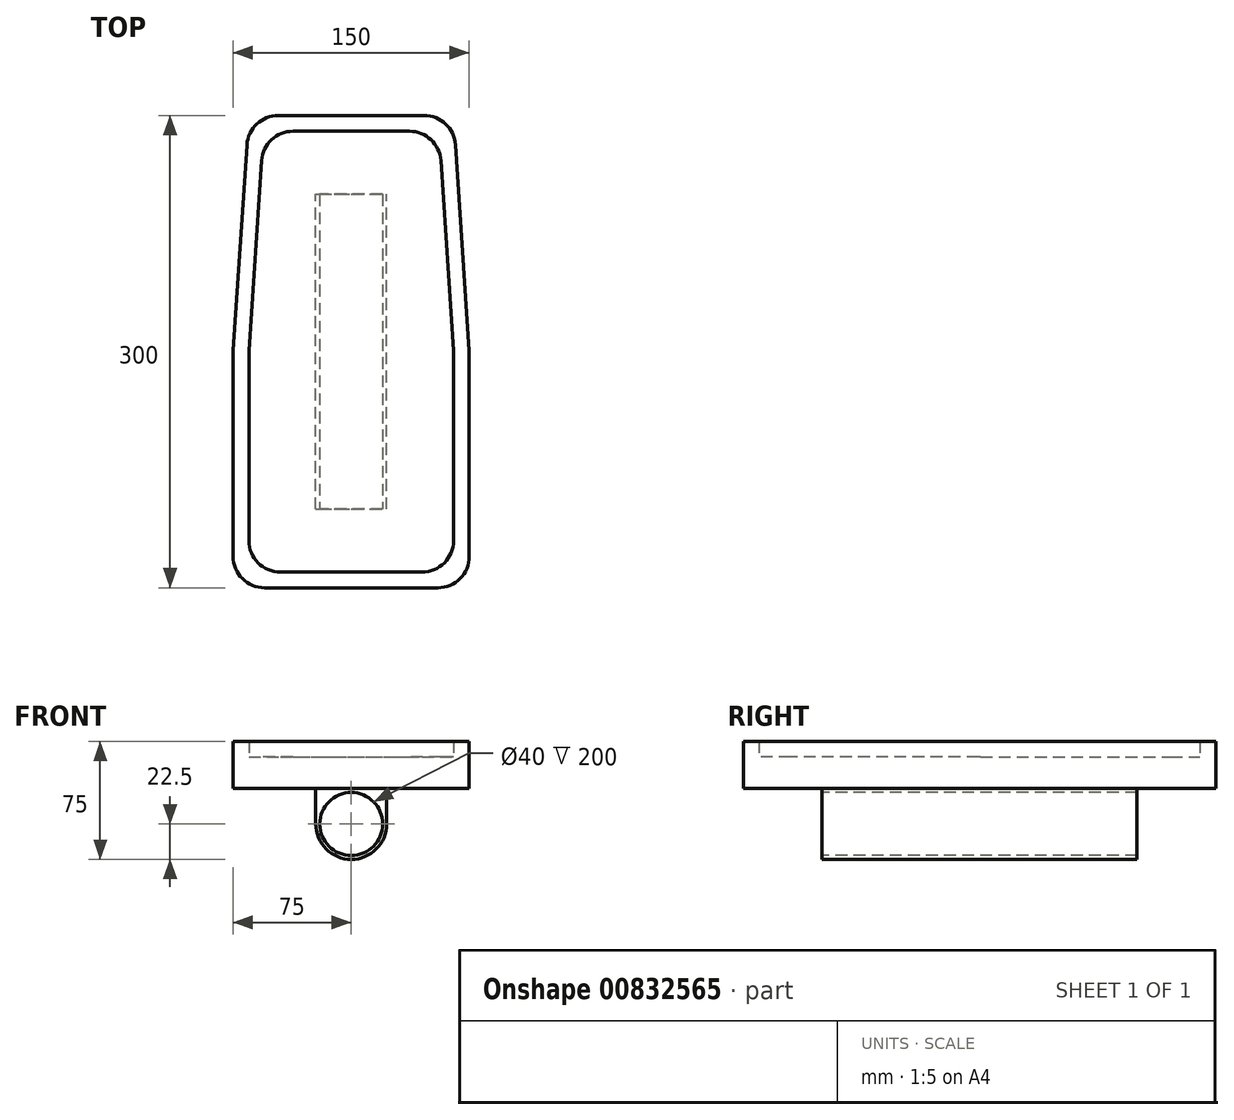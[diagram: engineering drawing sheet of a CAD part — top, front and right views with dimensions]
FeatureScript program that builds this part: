
annotation { "Feature Type Name" : "Feature", "Feature Type Description" : "" }
export const myFeature = defineFeature(function(context is Context, id is Id, definition is map)
    precondition{}
    {
        {
            var Q0;
            Q0=qCreatedBy(makeId("Top.planeOp"),FACE);
            var sketch = newSketch(context, id + "F0", { "sketchPlane" : qUnion([Q0])});
            skLineSegment(sketch, "E0.bottom", {"start": v(-65, 150) * mm, "end": v(65, 150) * mm});
            skLineSegment(sketch, "E0.top", {"start": v(-75, -150) * mm, "end": v(75, -150) * mm});
            skLineSegment(sketch, "E0.left", {"start": v(-75, 0) * mm, "end": v(-75, -150) * mm});
            skLineSegment(sketch, "E0.right", {"start": v(75, 0) * mm, "end": v(75, -150) * mm});
            skLineSegment(sketch, "E1.bottom", {"start": v(-55.67, 140) * mm, "end": v(55.67, 140) * mm});
            skLineSegment(sketch, "E1.top", {"start": v(-65, -140) * mm, "end": v(65, -140) * mm});
            skLineSegment(sketch, "E1.left", {"start": v(-65, 0) * mm, "end": v(-65, -140) * mm});
            skLineSegment(sketch, "E1.right", {"start": v(65, 0) * mm, "end": v(65, -140) * mm});
            skLineSegment(sketch, "E2", {"start": v(-75, 0) * mm, "end": v(-65, 150) * mm});
            skPoint(sketch, "E2.endSnap0", {"position": v(-65, 0) * mm});
            skLineSegment(sketch, "E3", {"start": v(75, 0) * mm, "end": v(65, 150) * mm});
            skPoint(sketch, "E4.orphan", {"position": v(-75, 150) * mm});
            skPoint(sketch, "E5.orphan", {"position": v(75, 150) * mm});
            skPoint(sketch, "E6.orphan", {"position": v(-65, 140) * mm});
            skPoint(sketch, "E7.orphan", {"position": v(65, 140) * mm});
            skPoint(sketch, "E8.0.start.orphan", {"position": v(-45, 140) * mm});
            skPoint(sketch, "E9.0.start.orphan", {"position": v(45, 140) * mm});
            skPoint(sketch, "E10.orphan", {"position": v(45, 150) * mm});
            skPoint(sketch, "E11.orphan", {"position": v(-45, 150) * mm});
            skLineSegment(sketch, "E12", {"start": v(65, 0) * mm, "end": v(55.67, 140) * mm});
            skLineSegment(sketch, "E13", {"start": v(-65, 0) * mm, "end": v(-55.67, 140) * mm});
            skSolve(sketch);
        }
        {
            var Q0;
            Q0=makeQuery(id+"F0.imprint","IMPRINT",FACE,{"disambiguationData":[TD([[makeQuery(id+"F0.imprint","IMPRINT",EDGE,{"derivedFrom":sQuery(id+"F0.wireOp",EDGE,"E0.bottom")}),-1.0]])]});
            extrude(context, id + "F1", {"entities" : qUnion([Q0]), "depth" : 30 * mm, "offsetDistance" : 25 * mm});
        }
        {
            var Q0;
            Q0=makeQuery(id+"F0.imprint","IMPRINT",FACE,{"disambiguationData":[TD([[makeQuery(id+"F0.imprint","IMPRINT",EDGE,{"derivedFrom":sQuery(id+"F0.wireOp",EDGE,"E1.bottom")}),-1.0]])]});
            extrude(context, id + "F2", {"entities" : qUnion([Q0]), "operationType" : NewBodyOperationType.ADD, "depth" : 20 * mm, "offsetDistance" : 25 * mm});
        }
        {
            var Q0;
            Q0=makeQuery(id+"F1.opExtrude","SWEPT_EDGE",EDGE,{"disambiguationData":[OSD([sQuery(id+"F0.wireOp",EDGE,"E0.bottom"),sQuery(id+"F0.wireOp",EDGE,"E0.left")])]});
            var Q1;
            Q1=makeQuery(id+"F1.opExtrude","SWEPT_EDGE",EDGE,{"disambiguationData":[OSD([sQuery(id+"F0.wireOp",EDGE,"E0.bottom"),sQuery(id+"F0.wireOp",EDGE,"E0.right")])]});
            var Q2;
            Q2=makeQuery(id+"F1.opExtrude","SWEPT_EDGE",EDGE,{"disambiguationData":[OSD([sQuery(id+"F0.wireOp",EDGE,"E0.top"),sQuery(id+"F0.wireOp",EDGE,"E0.right")])]});
            var Q3;
            Q3=makeQuery(id+"F1.opExtrude","SWEPT_EDGE",EDGE,{"disambiguationData":[OSD([sQuery(id+"F0.wireOp",EDGE,"E0.top"),sQuery(id+"F0.wireOp",EDGE,"E0.left")])]});
            fillet(context, id + "F3", {"entities" : qUnion([Q0, Q1, Q2, Q3]), "radius" : 20 * mm, "tangentPropagation" : true, "allowEdgeOverflow" : false});
        }
        {
            var Q0;
            Q0=makeQuery(id+"F1.opExtrude","SWEPT_EDGE",EDGE,{"disambiguationData":[OSD([sQuery(id+"F0.wireOp",EDGE,"E1.bottom"),sQuery(id+"F0.wireOp",EDGE,"E1.right")])]});
            var Q1;
            Q1=makeQuery(id+"F1.opExtrude","SWEPT_EDGE",EDGE,{"disambiguationData":[OSD([sQuery(id+"F0.wireOp",EDGE,"E1.top"),sQuery(id+"F0.wireOp",EDGE,"E1.right")])]});
            var Q2;
            Q2=makeQuery(id+"F1.opExtrude","SWEPT_EDGE",EDGE,{"disambiguationData":[OSD([sQuery(id+"F0.wireOp",EDGE,"E1.top"),sQuery(id+"F0.wireOp",EDGE,"E1.left")])]});
            var Q3;
            Q3=makeQuery(id+"F1.opExtrude","SWEPT_EDGE",EDGE,{"disambiguationData":[OSD([sQuery(id+"F0.wireOp",EDGE,"E1.bottom"),sQuery(id+"F0.wireOp",EDGE,"E1.left")])]});
            fillet(context, id + "F4", {"entities" : qUnion([Q0, Q1, Q2, Q3]), "radius" : 20 * mm, "tangentPropagation" : true, "allowEdgeOverflow" : false});
        }
        {
            var Q0;
            Q0=makeQuery(id+"F0.imprint","IMPRINT",FACE,{"disambiguationData":[TD([[makeQuery(id+"F0.imprint","IMPRINT",EDGE,{"derivedFrom":sQuery(id+"F0.wireOp",EDGE,"E1.bottom")}),-1.0]])]});
            var sketch = newSketch(context, id + "F5", { "sketchPlane" : qUnion([Q0])});
            skLineSegment(sketch, "E14.bottom", {"start": v(-22.5, -100) * mm, "end": v(22.5, -100) * mm});
            skLineSegment(sketch, "E14.top", {"start": v(-22.5, 100) * mm, "end": v(22.5, 100) * mm});
            skLineSegment(sketch, "E14.left", {"start": v(-22.5, -100) * mm, "end": v(-22.5, 100) * mm});
            skLineSegment(sketch, "E14.right", {"start": v(22.5, -100) * mm, "end": v(22.5, 100) * mm});
            skSolve(sketch);
        }
        {
            var Q0;
            Q0=makeQuery(id+"F5.imprint","IMPRINT",FACE,{"disambiguationData":[TD([[makeQuery(id+"F5.imprint","IMPRINT",EDGE,{"derivedFrom":sQuery(id+"F5.wireOp",EDGE,"E14.bottom")}),1.0]])]});
            extrude(context, id + "F6", {"entities" : qUnion([Q0]), "operationType" : NewBodyOperationType.ADD, "oppositeDirection" : true, "depth" : 45 * mm, "offsetDistance" : 25 * mm});
        }
        {
            var Q0;
            Q0=makeQuery(id+"F6.opExtrude","SWEPT_FACE",FACE,{"disambiguationData":[OSD([sQuery(id+"F5.wireOp",EDGE,"E14.bottom")])]});
            var sketch = newSketch(context, id + "F7", { "sketchPlane" : qUnion([Q0])});
            skCircle(sketch, "E15", {"center": v(0, -22.5) * mm, "radius": 20 * mm});
            skSolve(sketch);
        }
        {
            var Q0;
            Q0=makeQuery(id+"F7.imprint","IMPRINT",FACE,{"disambiguationData":[TD([[makeQuery(id+"F7.imprint","IMPRINT",EDGE,{"derivedFrom":sQuery(id+"F7.wireOp",EDGE,"E15")}),1.0]])]});
            extrude(context, id + "F8", {"entities" : qUnion([Q0]), "operationType" : NewBodyOperationType.REMOVE, "endBound" : BoundingType.UP_TO_NEXT, "oppositeDirection" : true, "depth" : 25 * mm, "offsetDistance" : 25 * mm});
        }
        {
            var Q0;
            Q0=makeQuery(id+"F6.opExtrude","CAP_EDGE",EDGE,{"disambiguationData":[OSD([sQuery(id+"F5.wireOp",EDGE,"E14.left")])],"isStart":false});
            var Q1;
            Q1=makeQuery(id+"F6.opExtrude","CAP_EDGE",EDGE,{"disambiguationData":[OSD([sQuery(id+"F5.wireOp",EDGE,"E14.right")])],"isStart":false});
            fillet(context, id + "F9", {"entities" : qUnion([Q0, Q1]), "radius" : 22.5 * mm, "tangentPropagation" : true, "allowEdgeOverflow" : false});
        }
    });
